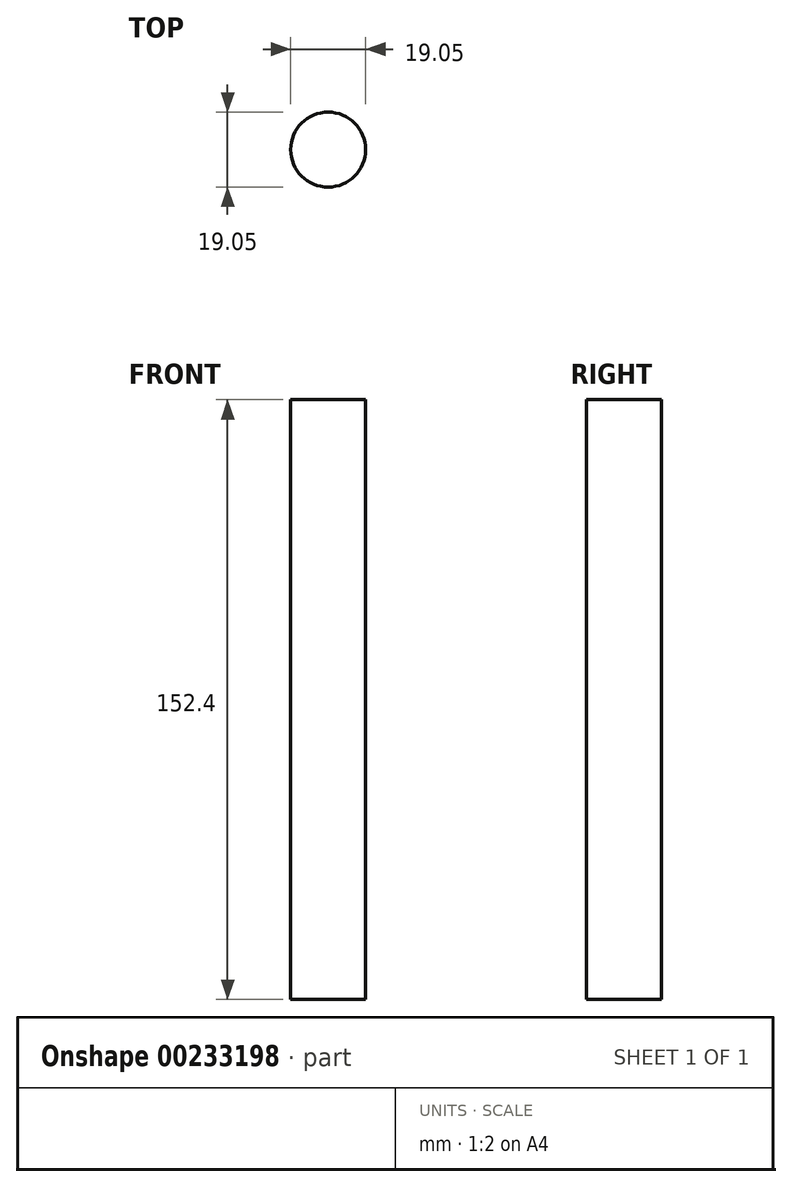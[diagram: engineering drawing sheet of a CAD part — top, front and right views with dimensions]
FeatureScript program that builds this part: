
annotation { "Feature Type Name" : "Feature", "Feature Type Description" : "" }
export const myFeature = defineFeature(function(context is Context, id is Id, definition is map)
    precondition{}
    {
        {
            var Q0;
            Q0=qCreatedBy(makeId("Top.planeOp"),FACE);
            var sketch = newSketch(context, id + "F0", { "sketchPlane" : qUnion([Q0])});
            skCircle(sketch, "E0", {"center": v(-14.2, 16) * mm, "radius": 9.53 * mm});
            skSolve(sketch);
        }
        {
            var Q0;
            Q0 = qSketchRegion(id + "F0", true);
            extrude(context, id + "F1", {"entities" : qUnion([Q0]), "depth" : 152.4 * mm});
        }
    });
